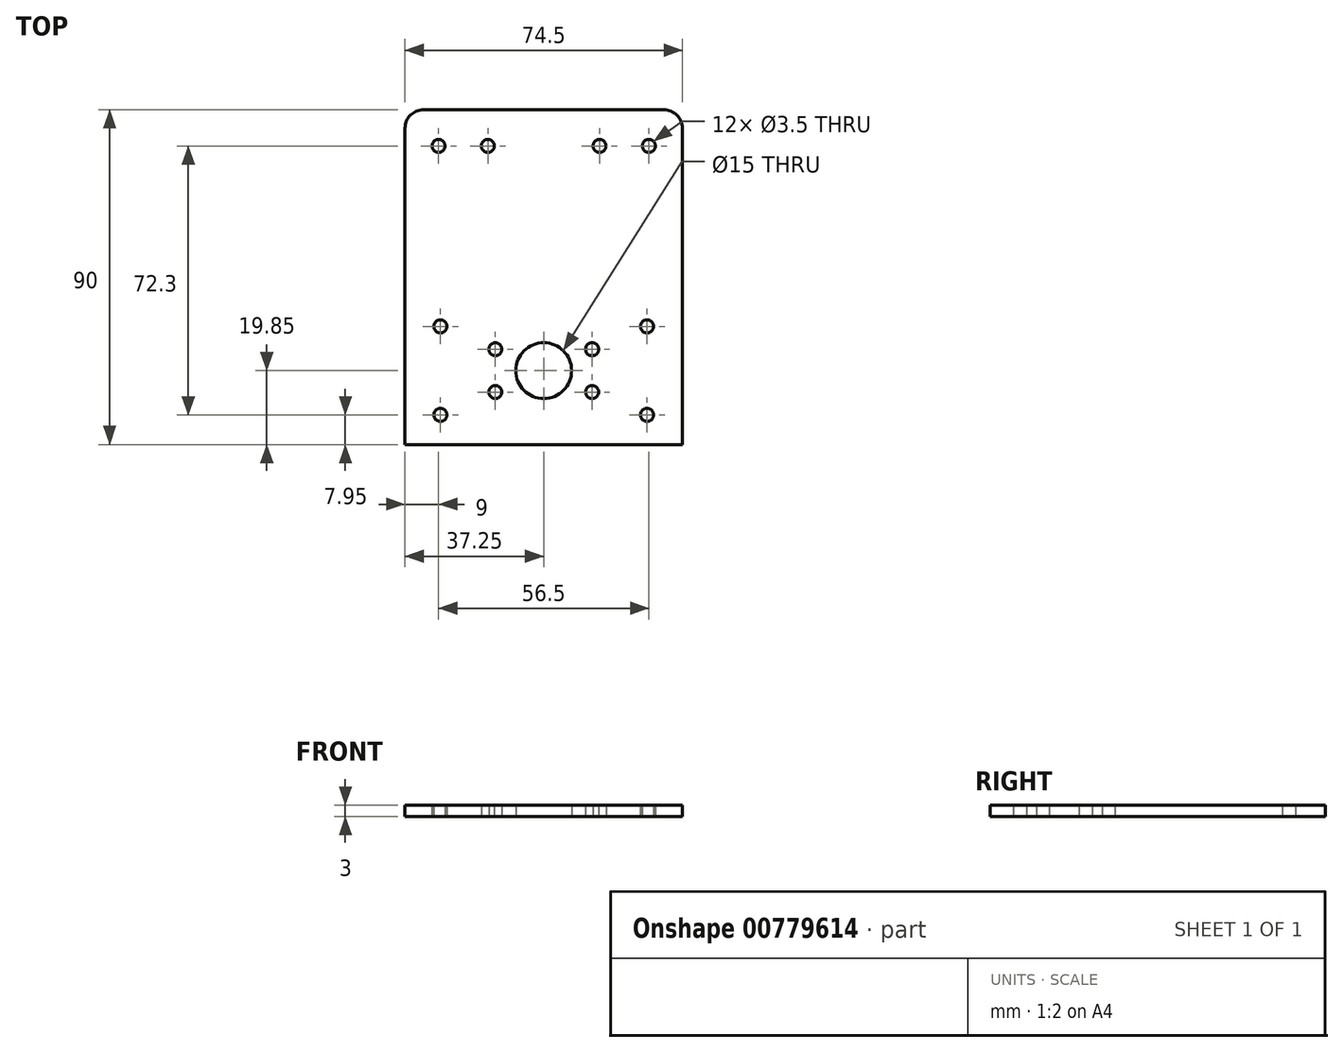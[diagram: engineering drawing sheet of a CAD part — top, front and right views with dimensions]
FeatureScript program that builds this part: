
annotation { "Feature Type Name" : "Feature", "Feature Type Description" : "" }
export const myFeature = defineFeature(function(context is Context, id is Id, definition is map)
    precondition{}
    {
        {
            var Q0;
            Q0=qCreatedBy(makeId("Top.planeOp"),FACE);
            var sketch = newSketch(context, id + "F0", { "sketchPlane" : qUnion([Q0])});
            skLineSegment(sketch, "E0.bottom", {"start": v(37.25, -45) * mm, "end": v(-37.25, -45) * mm});
            skLineSegment(sketch, "E0.top", {"start": v(32.25, 45) * mm, "end": v(-32.25, 45) * mm});
            skLineSegment(sketch, "E0.left", {"start": v(37.25, -45) * mm, "end": v(37.25, 40) * mm});
            skLineSegment(sketch, "E0.right", {"start": v(-37.25, -45) * mm, "end": v(-37.25, 40) * mm});
            skPoint(sketch, "E0.middle", {"position": v(0, 0) * mm});
            skPoint(sketch, "E1.visualSharp", {"position": v(-37.25, 45) * mm});
            skArc(sketch, "E1.filletArc", {"start": v(-32.25, 45) * mm, "mid": v(-35.79, 43.54) * mm, "end": v(-37.25, 40) * mm});
            skPoint(sketch, "E2.visualSharp", {"position": v(37.25, 45) * mm});
            skArc(sketch, "E2.filletArc", {"start": v(37.25, 40) * mm, "mid": v(35.79, 43.54) * mm, "end": v(32.25, 45) * mm});
            skPoint(sketch, "E3.visualSharp", {"position": v(37.25, -45) * mm});
            skPoint(sketch, "E4.visualSharp", {"position": v(-37.25, -45) * mm});
            skCircle(sketch, "E5", {"center": v(15, 35.25) * mm, "radius": 1.75 * mm});
            skCircle(sketch, "E6", {"center": v(27.75, -13.25) * mm, "radius": 1.75 * mm});
            skCircle(sketch, "E7", {"center": v(27.75, -37.05) * mm, "radius": 1.75 * mm});
            skCircle(sketch, "E8", {"center": v(28.25, 35.25) * mm, "radius": 1.75 * mm});
            skCircle(sketch, "E9", {"center": v(0, -25.15) * mm, "radius": 7.5 * mm});
            skCircle(sketch, "E10", {"center": v(13, -19.4) * mm, "radius": 1.75 * mm});
            skCircle(sketch, "E11", {"center": v(13, -30.9) * mm, "radius": 1.75 * mm});
            skCircle(sketch, "E12.MirrorC", {"center": v(-15, 35.25) * mm, "radius": 1.75 * mm});
            skCircle(sketch, "E13.MirrorC", {"center": v(-28.25, 35.25) * mm, "radius": 1.75 * mm});
            skCircle(sketch, "E14.MirrorC", {"center": v(-13, -19.4) * mm, "radius": 1.75 * mm});
            skCircle(sketch, "E15.MirrorC", {"center": v(-13, -30.9) * mm, "radius": 1.75 * mm});
            skCircle(sketch, "E16.MirrorC", {"center": v(-27.75, -37.05) * mm, "radius": 1.75 * mm});
            skCircle(sketch, "E17.MirrorC", {"center": v(-27.75, -13.25) * mm, "radius": 1.75 * mm});
            skLineSegment(sketch, "E18", {"start": v(-27.75, -13.25) * mm, "end": v(-27.75, -37.05) * mm, "construction": true});
            skLineSegment(sketch, "E19", {"start": v(-27.75, -25.15) * mm, "end": v(0, -25.15) * mm, "construction": true});
            skLineSegment(sketch, "E20", {"start": v(-13, -29.15) * mm, "end": v(13, -29.15) * mm, "construction": true});
            skSolve(sketch);
        }
        {
            var Q0;
            Q0 = qSketchRegion(id + "F0", true);
            extrude(context, id + "F1", {"entities" : qUnion([Q0]), "depth" : 3 * mm, "offsetDistance" : 25 * mm});
        }
    });
